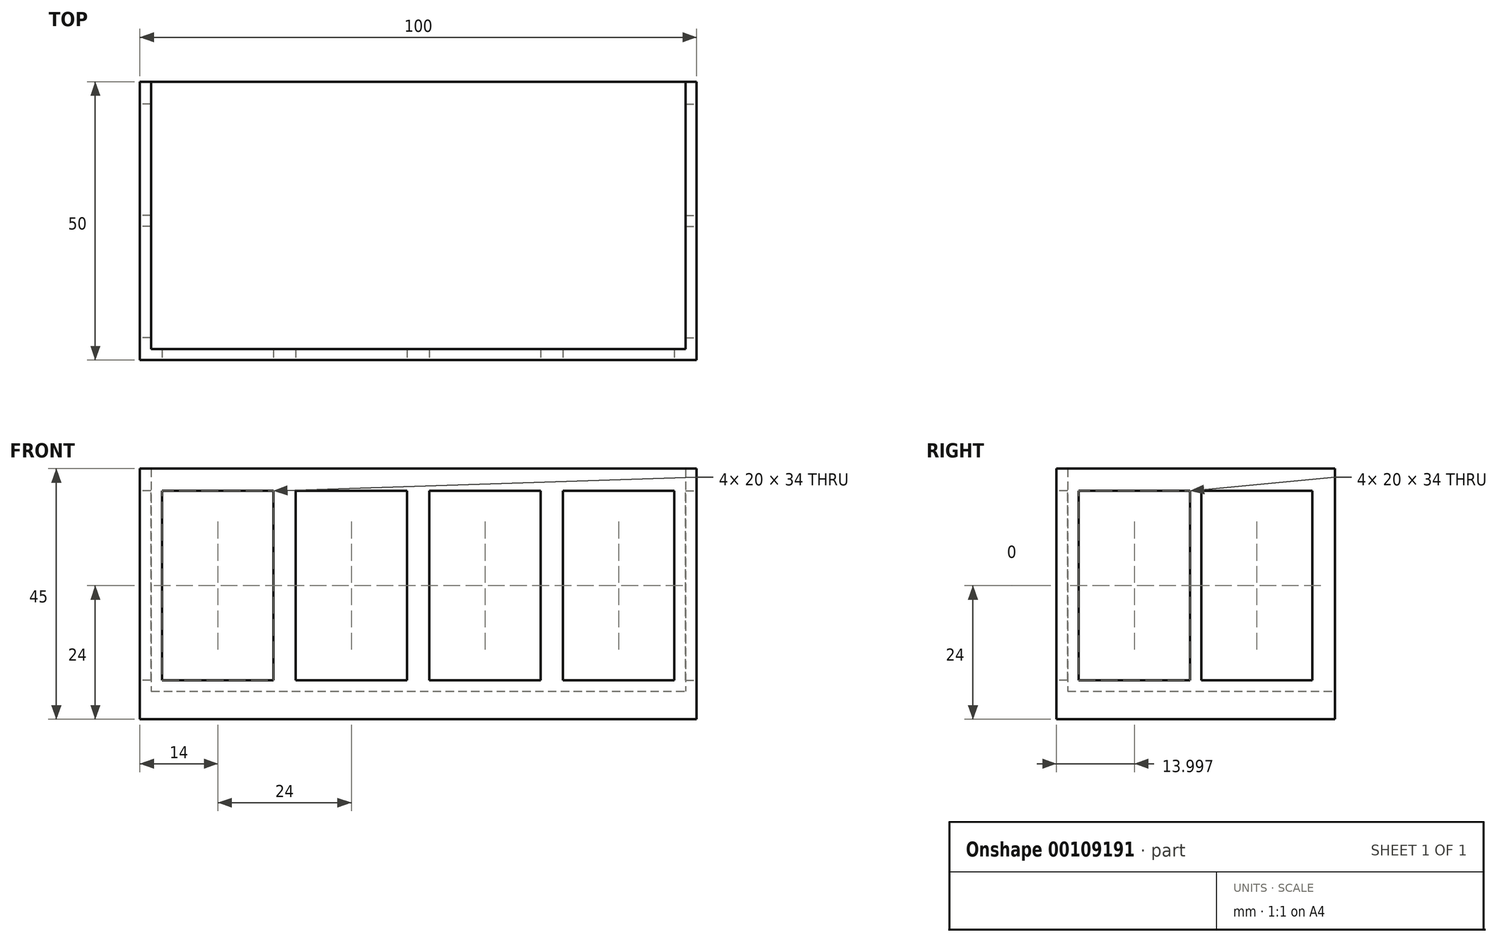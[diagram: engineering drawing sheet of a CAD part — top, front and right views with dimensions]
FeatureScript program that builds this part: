
annotation { "Feature Type Name" : "Feature", "Feature Type Description" : "" }
export const myFeature = defineFeature(function(context is Context, id is Id, definition is map)
    precondition{}
    {
        {
            var Q0;
            Q0=qCreatedBy(makeId("Top.planeOp"),FACE);
            var sketch = newSketch(context, id + "F0", { "sketchPlane" : qUnion([Q0])});
            skLineSegment(sketch, "E0.bottom", {"start": v(-30.98, 33.89) * mm, "end": v(69.02, 33.89) * mm});
            skLineSegment(sketch, "E0.top", {"start": v(-30.98, -16.11) * mm, "end": v(69.02, -16.11) * mm});
            skLineSegment(sketch, "E0.left", {"start": v(-30.98, 33.89) * mm, "end": v(-30.98, -16.11) * mm});
            skLineSegment(sketch, "E0.right", {"start": v(69.02, 33.89) * mm, "end": v(69.02, -16.11) * mm});
            skSolve(sketch);
        }
        {
            var Q0;
            Q0 = qSketchRegion(id + "F0", true);
            var Q1;
            Q1=makeQuery(id+"F0.imprint","IMPRINT",FACE,{"disambiguationData":[TD([[makeQuery(id+"F0.imprint","IMPRINT",EDGE,{"derivedFrom":sQuery(id+"F0.wireOp",EDGE,"E0.bottom")}),-1.0]])]});
            extrude(context, id + "F1", {"entities" : qUnion([Q0, Q1]), "depth" : 5 * mm});
        }
        {
            var Q0;
            Q0=makeQuery(id+"F1.opExtrude","CAP_FACE",FACE,{"disambiguationData":[OSD([sQuery(id+"F0.wireOp",EDGE,"E0.bottom"),sQuery(id+"F0.wireOp",EDGE,"E0.top"),sQuery(id+"F0.wireOp",EDGE,"E0.left"),sQuery(id+"F0.wireOp",EDGE,"E0.right")])],"isStart":false});
            var sketch = newSketch(context, id + "F2", { "sketchPlane" : qUnion([Q0])});
            skLineSegment(sketch, "E1.bottom", {"start": v(-30.98, 33.89) * mm, "end": v(-28.98, 33.89) * mm});
            skLineSegment(sketch, "E1.top", {"start": v(-30.98, -16.11) * mm, "end": v(-28.98, -16.11) * mm});
            skLineSegment(sketch, "E1.left", {"start": v(-30.98, 33.89) * mm, "end": v(-30.98, -16.11) * mm});
            skLineSegment(sketch, "E1.right", {"start": v(-28.98, 33.89) * mm, "end": v(-28.98, -16.11) * mm});
            skLineSegment(sketch, "E2.bottom", {"start": v(-28.98, -14.11) * mm, "end": v(69.02, -14.11) * mm});
            skLineSegment(sketch, "E2.top", {"start": v(-28.98, -16.11) * mm, "end": v(69.02, -16.11) * mm});
            skLineSegment(sketch, "E2.left", {"start": v(-28.98, -14.11) * mm, "end": v(-28.98, -16.11) * mm});
            skLineSegment(sketch, "E2.right", {"start": v(69.02, -14.11) * mm, "end": v(69.02, -16.11) * mm});
            skLineSegment(sketch, "E3.bottom", {"start": v(67.02, -14.11) * mm, "end": v(69.02, -14.11) * mm});
            skLineSegment(sketch, "E3.top", {"start": v(67.02, 33.89) * mm, "end": v(69.02, 33.89) * mm});
            skLineSegment(sketch, "E3.left", {"start": v(67.02, -14.11) * mm, "end": v(67.02, 33.89) * mm});
            skLineSegment(sketch, "E3.right", {"start": v(69.02, -14.11) * mm, "end": v(69.02, 33.89) * mm});
            skSolve(sketch);
        }
        {
            var Q0;
            Q0 = qSketchRegion(id + "F2", true);
            extrude(context, id + "F3", {"entities" : qUnion([Q0]), "operationType" : NewBodyOperationType.ADD, "depth" : 40 * mm});
        }
        {
            var Q0;
            Q0=makeQuery(id+"F3.boolean.opBoolean","MERGE",FACE,{"derivedFrom":[makeQuery(id+"F1.opExtrude","SWEPT_FACE",FACE,{"disambiguationData":[OSD([sQuery(id+"F0.wireOp",EDGE,"E0.top")])]}),makeQuery(id+"F3.opExtrude","SWEPT_FACE",FACE,{"disambiguationData":[OSD([sQuery(id+"F2.wireOp",EDGE,"E1.top"),sQuery(id+"F2.wireOp",EDGE,"E2.top")])]})]});
            var sketch = newSketch(context, id + "F4", { "sketchPlane" : qUnion([Q0])});
            skLineSegment(sketch, "E4.bottom", {"start": v(-26.98, 41) * mm, "end": v(-6.98, 41) * mm});
            skLineSegment(sketch, "E4.top", {"start": v(-26.98, 7) * mm, "end": v(-6.98, 7) * mm});
            skLineSegment(sketch, "E4.left", {"start": v(-26.98, 41) * mm, "end": v(-26.98, 7) * mm});
            skLineSegment(sketch, "E4.right", {"start": v(-6.98, 41) * mm, "end": v(-6.98, 7) * mm});
            skLineSegment(sketch, "E5.bottom", {"start": v(-2.98, 41) * mm, "end": v(17.02, 41) * mm});
            skLineSegment(sketch, "E5.top", {"start": v(-2.98, 7) * mm, "end": v(17.02, 7) * mm});
            skLineSegment(sketch, "E5.left", {"start": v(-2.98, 41) * mm, "end": v(-2.98, 7) * mm});
            skLineSegment(sketch, "E5.right", {"start": v(17.02, 41) * mm, "end": v(17.02, 7) * mm});
            skLineSegment(sketch, "E6.bottom", {"start": v(21.02, 41) * mm, "end": v(41.02, 41) * mm});
            skLineSegment(sketch, "E6.top", {"start": v(21.02, 7) * mm, "end": v(41.02, 7) * mm});
            skLineSegment(sketch, "E6.left", {"start": v(21.02, 41) * mm, "end": v(21.02, 7) * mm});
            skLineSegment(sketch, "E6.right", {"start": v(41.02, 41) * mm, "end": v(41.02, 7) * mm});
            skLineSegment(sketch, "E7.bottom", {"start": v(45.02, 41) * mm, "end": v(65.02, 41) * mm});
            skLineSegment(sketch, "E7.top", {"start": v(45.02, 7) * mm, "end": v(65.02, 7) * mm});
            skLineSegment(sketch, "E7.left", {"start": v(45.02, 41) * mm, "end": v(45.02, 7) * mm});
            skLineSegment(sketch, "E7.right", {"start": v(65.02, 41) * mm, "end": v(65.02, 7) * mm});
            skSolve(sketch);
        }
        {
            var Q0;
            Q0=makeQuery(id+"F4.imprint","IMPRINT",FACE,{"disambiguationData":[TD([[makeQuery(id+"F4.imprint","IMPRINT",EDGE,{"derivedFrom":sQuery(id+"F4.wireOp",EDGE,"E4.bottom")}),-1.0]])]});
            var Q1;
            Q1=makeQuery(id+"F4.imprint","IMPRINT",FACE,{"disambiguationData":[TD([[makeQuery(id+"F4.imprint","IMPRINT",EDGE,{"derivedFrom":sQuery(id+"F4.wireOp",EDGE,"E5.bottom")}),-1.0]])]});
            var Q2;
            Q2=makeQuery(id+"F4.imprint","IMPRINT",FACE,{"disambiguationData":[TD([[makeQuery(id+"F4.imprint","IMPRINT",EDGE,{"derivedFrom":sQuery(id+"F4.wireOp",EDGE,"E6.bottom")}),-1.0]])]});
            var Q3;
            Q3=makeQuery(id+"F4.imprint","IMPRINT",FACE,{"disambiguationData":[TD([[makeQuery(id+"F4.imprint","IMPRINT",EDGE,{"derivedFrom":sQuery(id+"F4.wireOp",EDGE,"E7.bottom")}),-1.0]])]});
            extrude(context, id + "F5", {"entities" : qUnion([Q0, Q1, Q2, Q3]), "operationType" : NewBodyOperationType.REMOVE, "oppositeDirection" : true, "depth" : 5 * mm});
        }
        {
            var Q0;
            Q0=makeQuery(id+"F3.boolean.opBoolean","MERGE",FACE,{"derivedFrom":[makeQuery(id+"F1.opExtrude","SWEPT_FACE",FACE,{"disambiguationData":[OSD([sQuery(id+"F0.wireOp",EDGE,"E0.left")])]}),makeQuery(id+"F3.opExtrude","SWEPT_FACE",FACE,{"disambiguationData":[OSD([sQuery(id+"F2.wireOp",EDGE,"E1.left")])]})]});
            var sketch = newSketch(context, id + "F6", { "sketchPlane" : qUnion([Q0])});
            skLineSegment(sketch, "E8.bottom", {"start": v(-29.89, 41) * mm, "end": v(-9.89, 41) * mm});
            skLineSegment(sketch, "E8.top", {"start": v(-29.89, 7) * mm, "end": v(-9.89, 7) * mm});
            skLineSegment(sketch, "E8.left", {"start": v(-29.89, 41) * mm, "end": v(-29.89, 7) * mm});
            skLineSegment(sketch, "E8.right", {"start": v(-9.89, 41) * mm, "end": v(-9.89, 7) * mm});
            skLineSegment(sketch, "E9.bottom", {"start": v(-7.89, 41) * mm, "end": v(12.11, 41) * mm});
            skLineSegment(sketch, "E9.top", {"start": v(-7.89, 7) * mm, "end": v(12.11, 7) * mm});
            skLineSegment(sketch, "E9.left", {"start": v(-7.89, 41) * mm, "end": v(-7.89, 7) * mm});
            skLineSegment(sketch, "E9.right", {"start": v(12.11, 41) * mm, "end": v(12.11, 7) * mm});
            skSolve(sketch);
        }
        {
            var Q0;
            Q0 = qSketchRegion(id + "F6", true);
            var Q1;
            Q1=makeQuery(id+"F6.imprint","IMPRINT",FACE,{"disambiguationData":[TD([[makeQuery(id+"F6.imprint","IMPRINT",EDGE,{"derivedFrom":sQuery(id+"F6.wireOp",EDGE,"E8.bottom")}),-1.0]])]});
            var Q2;
            Q2=makeQuery(id+"F6.imprint","IMPRINT",FACE,{"disambiguationData":[TD([[makeQuery(id+"F6.imprint","IMPRINT",EDGE,{"derivedFrom":sQuery(id+"F6.wireOp",EDGE,"E9.bottom")}),-1.0]])]});
            extrude(context, id + "F7", {"entities" : qUnion([Q0, Q1, Q2]), "operationType" : NewBodyOperationType.REMOVE, "oppositeDirection" : true, "depth" : 5 * mm});
        }
        {
            var Q0;
            Q0=makeQuery(id+"F3.boolean.opBoolean","MERGE",FACE,{"derivedFrom":[makeQuery(id+"F1.opExtrude","SWEPT_FACE",FACE,{"disambiguationData":[OSD([sQuery(id+"F0.wireOp",EDGE,"E0.right")])]}),makeQuery(id+"F3.opExtrude","SWEPT_FACE",FACE,{"disambiguationData":[OSD([sQuery(id+"F2.wireOp",EDGE,"E2.right"),sQuery(id+"F2.wireOp",EDGE,"E3.right")])]})]});
            var sketch = newSketch(context, id + "F8", { "sketchPlane" : qUnion([Q0])});
            skLineSegment(sketch, "E10.bottom", {"start": v(-12.11, 41) * mm, "end": v(7.89, 41) * mm});
            skLineSegment(sketch, "E10.top", {"start": v(-12.11, 7) * mm, "end": v(7.89, 7) * mm});
            skLineSegment(sketch, "E10.left", {"start": v(-12.11, 41) * mm, "end": v(-12.11, 7) * mm});
            skLineSegment(sketch, "E10.right", {"start": v(7.89, 41) * mm, "end": v(7.89, 7) * mm});
            skLineSegment(sketch, "E11.bottom", {"start": v(29.89, 41) * mm, "end": v(9.89, 41) * mm});
            skLineSegment(sketch, "E11.top", {"start": v(29.89, 7) * mm, "end": v(9.89, 7) * mm});
            skLineSegment(sketch, "E11.left", {"start": v(29.89, 41) * mm, "end": v(29.89, 7) * mm});
            skLineSegment(sketch, "E11.right", {"start": v(9.89, 41) * mm, "end": v(9.89, 7) * mm});
            skSolve(sketch);
        }
        {
            var Q0;
            Q0=makeQuery(id+"F8.imprint","IMPRINT",FACE,{"disambiguationData":[TD([[makeQuery(id+"F8.imprint","IMPRINT",EDGE,{"derivedFrom":sQuery(id+"F8.wireOp",EDGE,"E10.bottom")}),-1.0]])]});
            var Q1;
            Q1=makeQuery(id+"F8.imprint","IMPRINT",FACE,{"disambiguationData":[TD([[makeQuery(id+"F8.imprint","IMPRINT",EDGE,{"derivedFrom":sQuery(id+"F8.wireOp",EDGE,"E11.bottom")}),1.0]])]});
            extrude(context, id + "F9", {"entities" : qUnion([Q0, Q1]), "operationType" : NewBodyOperationType.REMOVE, "oppositeDirection" : true, "depth" : 5 * mm});
        }
    });
